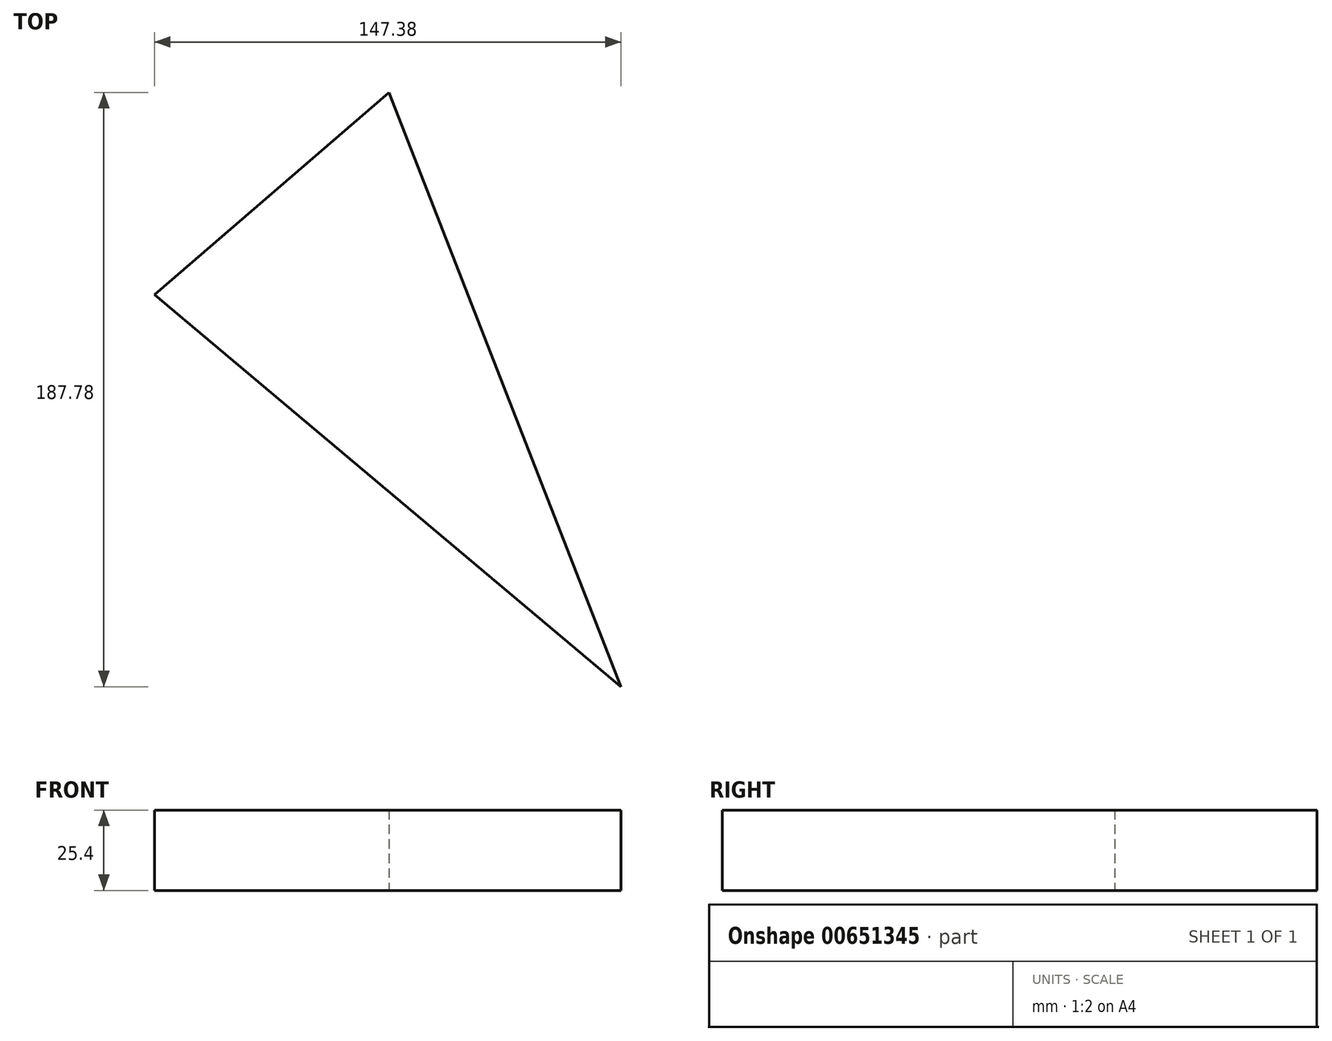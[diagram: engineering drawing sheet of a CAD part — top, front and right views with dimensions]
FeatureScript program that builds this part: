
annotation { "Feature Type Name" : "Feature", "Feature Type Description" : "" }
export const myFeature = defineFeature(function(context is Context, id is Id, definition is map)
    precondition{}
    {
        {
            var Q0;
            Q0=qCreatedBy(makeId("Top.planeOp"),FACE);
            var sketch = newSketch(context, id + "F0", { "sketchPlane" : qUnion([Q0])});
            skLineSegment(sketch, "E0", {"start": v(27.16, 25.98) * mm, "end": v(101.18, 89.9) * mm});
            skLineSegment(sketch, "E1", {"start": v(101.18, 89.9) * mm, "end": v(174.54, -97.88) * mm});
            skLineSegment(sketch, "E2", {"start": v(174.54, -97.88) * mm, "end": v(27.16, 25.98) * mm});
            skSolve(sketch);
        }
        {
            var Q0;
            Q0 = qSketchRegion(id + "F0", true);
            extrude(context, id + "F1", {"entities" : qUnion([Q0]), "depth" : 25.4 * mm, "offsetDistance" : 25.4 * mm});
        }
    });
